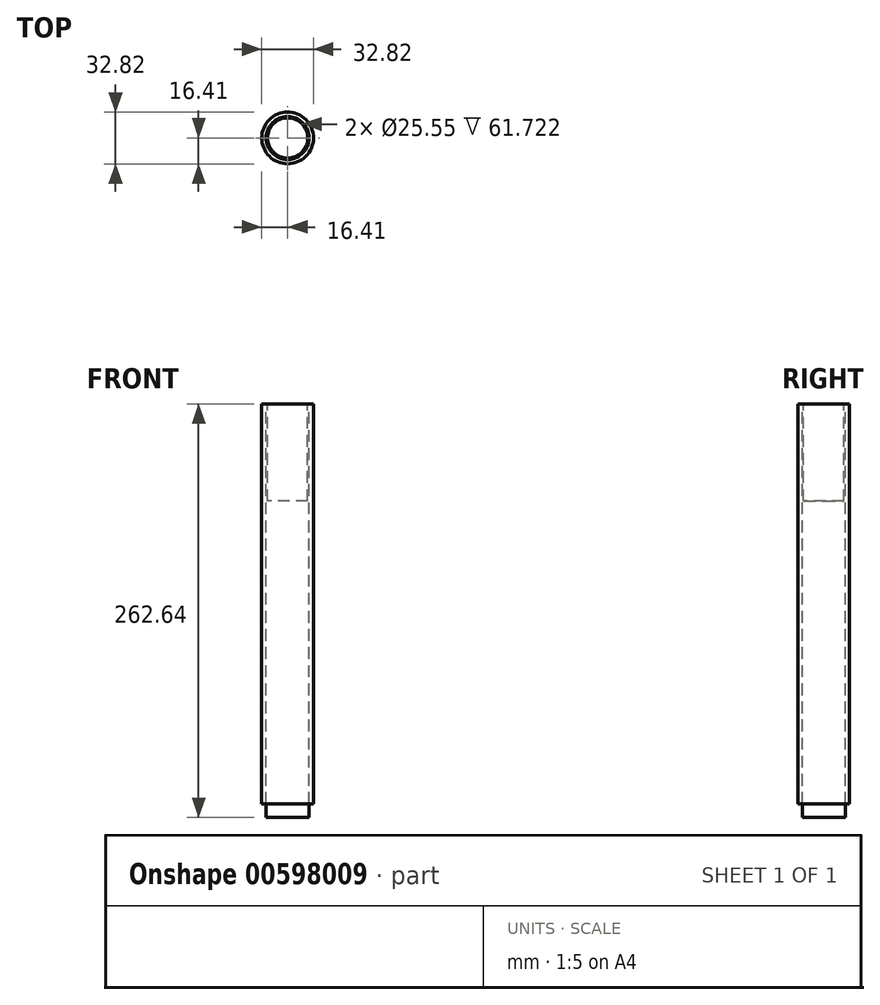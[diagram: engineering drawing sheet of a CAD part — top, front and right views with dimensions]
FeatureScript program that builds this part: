
annotation { "Feature Type Name" : "Feature", "Feature Type Description" : "" }
export const myFeature = defineFeature(function(context is Context, id is Id, definition is map)
    precondition{}
    {
        {
            var Q0;
            Q0=qCreatedBy(makeId("Top.planeOp"),FACE);
            var sketch = newSketch(context, id + "F0", { "sketchPlane" : qUnion([Q0])});
            skCircle(sketch, "E0", {"center": v(0, 0) * mm, "radius": 16.4 * mm});
            skCircle(sketch, "E1", {"center": v(0, 0) * mm, "radius": 12.77 * mm});
            skSolve(sketch);
        }
        {
            var Q0;
            Q0=makeQuery(id+"F0.imprint","IMPRINT",FACE,{"disambiguationData":[TD([[makeQuery(id+"F0.imprint","IMPRINT",EDGE,{"derivedFrom":sQuery(id+"F0.wireOp",EDGE,"E0")}),1.0]])]});
            var Q1;
            Q1=makeQuery(id+"F0.imprint","IMPRINT",FACE,{"disambiguationData":[TD([[makeQuery(id+"F0.imprint","IMPRINT",EDGE,{"derivedFrom":sQuery(id+"F0.wireOp",EDGE,"E1")}),1.0]])]});
            var Q2;
            Q2=sQuery(id+"F0.wireOp",EDGE,"E0");
            extrude(context, id + "F1", {"entities" : qUnion([Q0, Q1]), "surfaceEntities" : qUnion([Q2]), "oppositeDirection" : true, "depth" : 254 * mm, "offsetDistance" : 25.4 * mm});
        }
        {
            var Q0;
            Q0=qCreatedBy(makeId("Top.planeOp"),FACE);
            var sketch = newSketch(context, id + "F2", { "sketchPlane" : qUnion([Q0])});
            skCircle(sketch, "E2", {"center": v(0, 0) * mm, "radius": 13.62 * mm});
            skSolve(sketch);
        }
        {
            var Q0;
            Q0 = qSketchRegion(id + "F2", true);
            var Q1;
            Q1=sQuery(id+"F2.wireOp",EDGE,"E2");
            extrude(context, id + "F3", {"entities" : qUnion([Q0]), "surfaceEntities" : qUnion([Q1]), "oppositeDirection" : true, "depth" : 262.64 * mm, "offsetDistance" : 25.4 * mm});
        }
        {
            var Q0;
            Q0=makeQuery(id+"F0.imprint","IMPRINT",FACE,{"disambiguationData":[TD([[makeQuery(id+"F0.imprint","IMPRINT",EDGE,{"derivedFrom":sQuery(id+"F0.wireOp",EDGE,"E1")}),1.0]])]});
            extrude(context, id + "F4", {"entities" : qUnion([Q0]), "operationType" : NewBodyOperationType.REMOVE, "oppositeDirection" : true, "depth" : 61.72 * mm, "offsetDistance" : 25.4 * mm});
        }
        {
            var Q0;
            Q0=makeQuery(id+"F0.imprint","IMPRINT",FACE,{"disambiguationData":[TD([[makeQuery(id+"F0.imprint","IMPRINT",EDGE,{"derivedFrom":sQuery(id+"F0.wireOp",EDGE,"E1")}),1.0]])]});
            extrude(context, id + "F5", {"entities" : qUnion([Q0]), "operationType" : NewBodyOperationType.REMOVE, "oppositeDirection" : true, "depth" : 50.3 * mm, "offsetDistance" : 25.4 * mm});
        }
    });
